# Revit family: LeL Reiko 3.0
name_source: partatom
category: Lighting Fixtures
units: mm (PartAtom-declared; Revit-internal decimal feet)

## family parameters
Always vertical = No
Cut with Voids When Loaded = No
Light Source = No
OmniClass Number = 23.80.70.00
OmniClass Title = Lighting
Part Type = Normal
Room Calculation Point = No
Round Connector Dimension = Use Diameter
Shared = No
Work Plane-Based = Yes

## types (17) — shared parameters
CCT = 3000 K
CRI = CRI80
Default Elevation = 1219 mm
Description = Outdoor Projectors
IK = IK06
IP = IP66
Lamp = LED
Manufacturer = L&L Luce&Light srl
Model = RK30
Rated Power supply = 24 V
URL = https://www.lucelight.it
Weight = 1.25 kg

## per-type parameters (varying)
| type | Apparent Load | Lumen Output | Photometry | Wattage |
| K 54° 10W | 10 VA | 642 lm | RK30 Light source : K 54° 10W | 10 W |
| L 37° 10W | 10 VA | 702 lm | RK30 Light source : L 37° 10W | 10 W |
| M 30° 10W | 10 VA | 435 lm | RK30 Light source : M 30° 10W | 10 W |
| P (32°) 10W | 10 VA | 189 lm | RK30 Light source : P (32°) 10W | 10 W |
| P (32°) SHADOW 10W | 10 VA | 95 lm | RK30 Light source : P (32°) SHADOW 10W | 10 W |
| S 10° 10W | 10 VA | 498 lm | RK30 Light source : S 10° 10W | 10 W |
| V 8° 10W | 10 VA | 616 lm | RK30 Light source : V 8° 10W | 10 W |
| W 11°x60° 10W | 10 VA | 746 lm | RK30 Light source : W 11°x60° 10W | 10 W |
| X 27°x64° 10W | 10 VA | 541 lm | RK30 Light source : X 27°x64° 10W | 10 W |
| K 54° 15W | 15 VA | 1028 lm | RK30 Light source : K 54° 15W | 15 W |
| L 37° 15W | 15 VA | 1124 lm | RK30 Light source : L 37° 15W | 15 W |
| M 30° 15W | 15 VA | 697 lm | RK30 Light source : M 30° 15W | 15 W |
| P (32°) 15W | 15 VA | 303 lm | RK30 Light source : P (32°) 15W | 15 W |
| P (32°) SHADOW 15W | 15 VA | 153 lm | RK30 Light source : P (32°) SHADOW 15W | 15 W |
| S 10° 15W | 15 VA | 797 lm | RK30 Light source : S 10° 15W | 15 W |
| W 11°x60° 15W | 15 VA | 466 lm | RK30 Light source : W 11°x60° 15W | 15 W |
| X 27°x64° 15W | 15 VA | 338 lm | RK30 Light source : X 27°x64° 15W | 15 W |

## geometry (parser evidence)
native form markers: Sweep x4
no freeform markers — native parametric forms only
